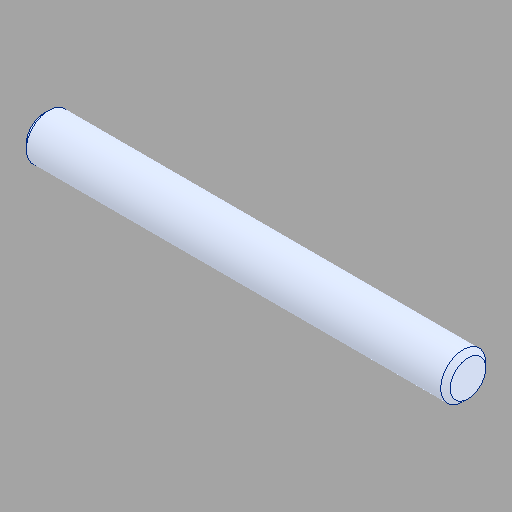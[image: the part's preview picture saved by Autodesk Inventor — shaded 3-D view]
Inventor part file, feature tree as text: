
AUTODESK INVENTOR PART (.ipt)
format: ipt  version: 2024.2 (Build 282272000, 272)  size: 90,112 bytes
history: native  units: in
note: dims shown in document units (in); Inventor stores cm internally (conversion verified against a paired STEP export)
features: chamfer x1
ambient origin geometry x8: Origin, YZ Plane, XZ Plane, XY Plane, X Axis, Y Axis, Z Axis, Center Point
bodies: Solid1 (feature_tree)
feature tree (1):
  chamfer  "Chamfer1"  [1 undecoded]
note: 1 required parameter value undecoded (feature->parameter linkage not recoverable at this tier; creation-order binding heuristic only, values carry confidence <= 0.55)
